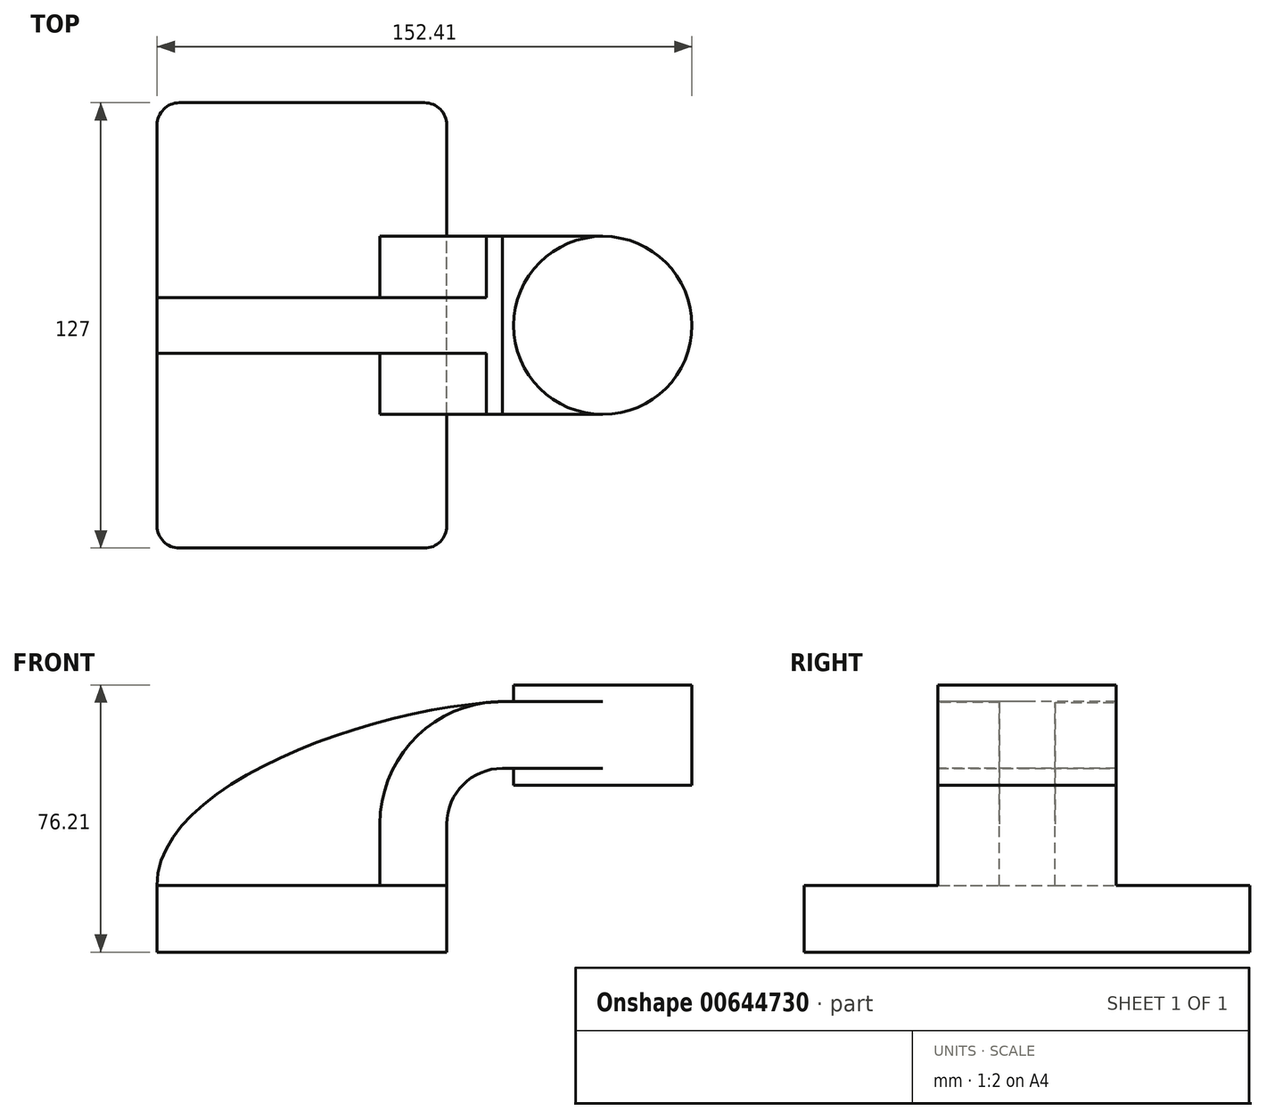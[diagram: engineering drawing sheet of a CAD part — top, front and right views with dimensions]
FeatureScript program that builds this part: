
annotation { "Feature Type Name" : "Feature", "Feature Type Description" : "" }
export const myFeature = defineFeature(function(context is Context, id is Id, definition is map)
    precondition{}
    {
        {
            var Q0;
            Q0=qCreatedBy(makeId("Front.planeOp"),FACE);
            var sketch = newSketch(context, id + "F0", { "sketchPlane" : qUnion([Q0])});
            skLineSegment(sketch, "E0.bottom", {"start": v(41.28, -9.52) * mm, "end": v(-41.28, -9.53) * mm});
            skLineSegment(sketch, "E0.top", {"start": v(41.28, 9.53) * mm, "end": v(-41.28, 9.53) * mm});
            skLineSegment(sketch, "E0.left", {"start": v(41.28, -9.52) * mm, "end": v(41.28, 9.53) * mm});
            skLineSegment(sketch, "E0.right", {"start": v(-41.28, -9.53) * mm, "end": v(-41.28, 9.53) * mm});
            skPoint(sketch, "E0.middle", {"position": v(0, 0) * mm});
            skLineSegment(sketch, "E1", {"start": v(41.28, 9.53) * mm, "end": v(41.28, 27) * mm});
            skLineSegment(sketch, "E2.bottom", {"start": v(60.32, 38.1) * mm, "end": v(111.12, 38.1) * mm});
            skLineSegment(sketch, "E2.top", {"start": v(60.32, 66.68) * mm, "end": v(111.12, 66.68) * mm});
            skLineSegment(sketch, "E2.left", {"start": v(60.32, 38.1) * mm, "end": v(60.32, 66.67) * mm});
            skLineSegment(sketch, "E2.right", {"start": v(111.12, 38.1) * mm, "end": v(111.12, 66.68) * mm});
            skPoint(sketch, "E2.middle", {"position": v(85.72, 52.39) * mm});
            skArc(sketch, "E3", {"start": v(41.27, 27) * mm, "mid": v(45.92, 38.23) * mm, "end": v(57.15, 42.88) * mm});
            skLineSegment(sketch, "E4", {"start": v(57.15, 42.88) * mm, "end": v(85.72, 42.88) * mm});
            skLineSegment(sketch, "E5.0", {"start": v(57.15, 61.93) * mm, "end": v(86.04, 61.93) * mm});
            skArc(sketch, "E5.1", {"start": v(22.23, 27) * mm, "mid": v(32.45, 51.7) * mm, "end": v(57.15, 61.93) * mm});
            skLineSegment(sketch, "E5.2", {"start": v(22.22, 9.53) * mm, "end": v(22.22, 27) * mm});
            skFitSpline(sketch, "E6", {"points": [v(-41.28, 9.53) * mm, v(57.15, 61.93) * mm], "startDerivative": vector(-1.19, 85.73) * mm, "endDerivative": vector(113.57, 5.31) * mm});
            skLineSegment(sketch, "E7", {"start": v(85.72, 38.1) * mm, "end": v(85.72, 66.68) * mm});
            skSolve(sketch);
        }
        {
            var Q0;
            Q0=makeQuery(id+"F0.imprint","IMPRINT",FACE,{"disambiguationData":[TD([[makeQuery(id+"F0.imprint","IMPRINT",EDGE,{"derivedFrom":sQuery(id+"F0.wireOp",EDGE,"E0.bottom")}),-1.0]])]});
            extrude(context, id + "F1", {"entities" : qUnion([Q0]), "endBound" : BoundingType.SYMMETRIC, "depth" : 127 * mm, "offsetDistance" : 25.4 * mm});
        }
        {
            var Q0;
            {var subQ1=sQuery(id+"F0.wireOp",EDGE,"E1");Q0=makeQuery(id+"F0.imprint","IMPRINT",FACE,{"disambiguationData":[TD([[makeQuery(id+"F0.imprint","IMPRINT",EDGE,{"derivedFrom":subQ1}),1.0]])]});}
            var Q1;
            {var subQ0=sQuery(id+"F0.wireOp",EDGE,"E4");var subQ1=sQuery(id+"F0.wireOp",EDGE,"E2.left");var subQ2=makeQuery(id+"F0.imprint","INTERSECT",VERTEX,{"derivedFrom":[subQ1,subQ0]});Q1=makeQuery(id+"F0.imprint","IMPRINT",FACE,{"disambiguationData":[TD([[makeQuery(id+"F0.imprint","IMPRINT",EDGE,{"disambiguationData":[TD([[subQ2,-1.0]])],"derivedFrom":subQ1}),-1.0]])]});}
            extrude(context, id + "F2", {"entities" : qUnion([Q0, Q1]), "operationType" : NewBodyOperationType.ADD, "endBound" : BoundingType.SYMMETRIC, "depth" : 50.8 * mm, "offsetDistance" : 25.4 * mm});
        }
        {
            var Q0;
            {var subQ3=sQuery(id+"F0.wireOp",EDGE,"E5.2");Q0=makeQuery(id+"F0.imprint","IMPRINT",FACE,{"disambiguationData":[TD([[makeQuery(id+"F0.imprint","IMPRINT",EDGE,{"derivedFrom":subQ3}),1.0]])]});}
            extrude(context, id + "F3", {"entities" : qUnion([Q0]), "operationType" : NewBodyOperationType.ADD, "endBound" : BoundingType.SYMMETRIC, "depth" : 15.88 * mm, "offsetDistance" : 25.4 * mm});
        }
        {
            var Q0;
            {var subQ0=sQuery(id+"F0.wireOp",EDGE,"E2.right");Q0=makeQuery(id+"F0.imprint","IMPRINT",FACE,{"disambiguationData":[TD([[makeQuery(id+"F0.imprint","IMPRINT",EDGE,{"derivedFrom":subQ0}),1.0]])]});}
            var Q1;
            Q1=sQuery(id+"F0.wireOp",EDGE,"E7");
            revolve(context, id + "F4", {"operationType" : NewBodyOperationType.ADD, "entities" : qUnion([Q0]), "axis" : qUnion([Q1]), "revolveType" : RevolveType.FULL});
        }
        {
            var Q0;
            Q0=makeQuery(id+"F1.opExtrude","CAP_EDGE",EDGE,{"disambiguationData":[OSD([sQuery(id+"F0.wireOp",EDGE,"E0.right")])],"isStart":true});
            var Q1;
            Q1=makeQuery(id+"F1.opExtrude","CAP_EDGE",EDGE,{"disambiguationData":[OSD([sQuery(id+"F0.wireOp",EDGE,"E0.right")])],"isStart":false});
            var Q2;
            Q2=makeQuery(id+"F1.opExtrude","CAP_EDGE",EDGE,{"disambiguationData":[OSD([sQuery(id+"F0.wireOp",EDGE,"E0.left")])],"isStart":false});
            var Q3;
            Q3=makeQuery(id+"F1.opExtrude","CAP_EDGE",EDGE,{"disambiguationData":[OSD([sQuery(id+"F0.wireOp",EDGE,"E0.left")])],"isStart":true});
            fillet(context, id + "F5", {"entities" : qUnion([Q0, Q1, Q2, Q3]), "radius" : 6.35 * mm, "tangentPropagation" : true, "allowEdgeOverflow" : false});
        }
    });
